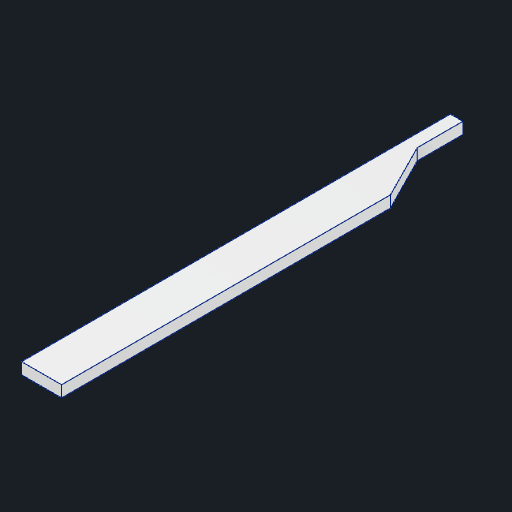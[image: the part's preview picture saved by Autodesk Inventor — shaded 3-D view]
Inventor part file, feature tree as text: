
AUTODESK INVENTOR PART (.ipt)
format: ipt  version: 2024 (Build 280153000, 153)  size: 90,112 bytes
history: native  units: in
note: dims shown in document units (in); Inventor stores cm internally (conversion verified against a paired STEP export)
features: other x3, sketch x3
ambient origin geometry x8: Origin, YZ Plane, XZ Plane, XY Plane, X Axis, Y Axis, Z Axis, Center Point
bodies: Solid1 (feature_tree)
feature tree (6):
  other  "YflanecYcrepA.ipt"
  other  "Solid1::YflanecYcrepA.ipt"
  other  "TaggingFeature1"
  sketch  "Sketch1"  dims[d0=0.3937in]
  sketch  "Sketch2"
  sketch  "Sketch3"
